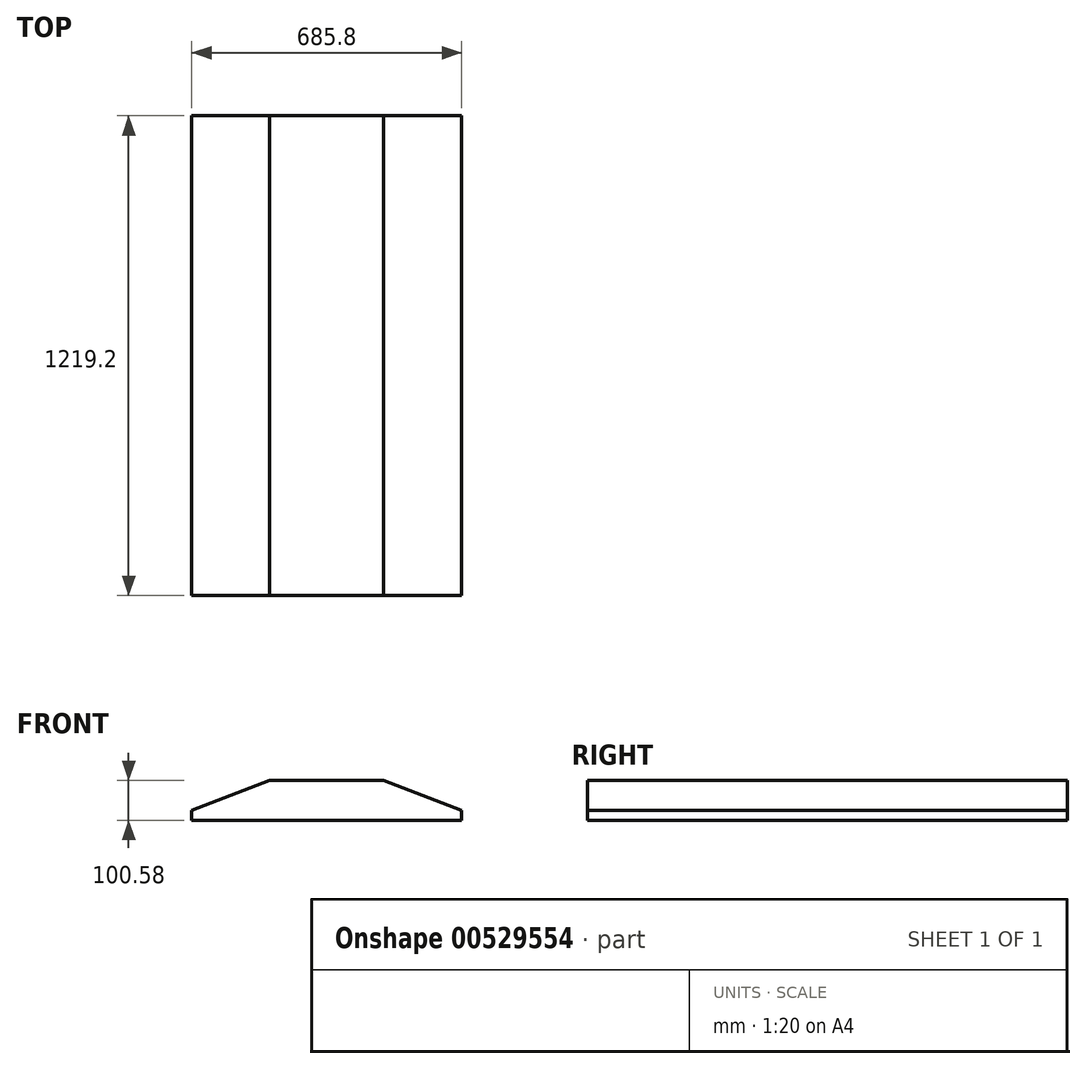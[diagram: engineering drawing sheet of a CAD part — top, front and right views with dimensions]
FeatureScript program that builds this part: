
annotation { "Feature Type Name" : "Feature", "Feature Type Description" : "" }
export const myFeature = defineFeature(function(context is Context, id is Id, definition is map)
    precondition{}
    {
        {
            var Q0;
            Q0=qCreatedBy(makeId("Top.planeOp"),FACE);
            var sketch = newSketch(context, id + "F0", { "sketchPlane" : qUnion([Q0])});
            skLineSegment(sketch, "E0.bottom", {"start": v(-362.06, 514.95) * mm, "end": v(323.74, 514.95) * mm});
            skLineSegment(sketch, "E0.top", {"start": v(-362.06, -704.25) * mm, "end": v(323.74, -704.25) * mm});
            skLineSegment(sketch, "E0.left", {"start": v(-362.06, 514.95) * mm, "end": v(-362.06, -704.25) * mm});
            skLineSegment(sketch, "E0.right", {"start": v(323.74, 514.95) * mm, "end": v(323.74, -704.25) * mm});
            skSolve(sketch);
        }
        {
            var Q0;
            Q0=makeQuery(id+"F0.imprint","IMPRINT",FACE,{"disambiguationData":[TD([[makeQuery(id+"F0.imprint","IMPRINT",EDGE,{"derivedFrom":sQuery(id+"F0.wireOp",EDGE,"E0.bottom")}),-1.0]])]});
            extrude(context, id + "F1", {"entities" : qUnion([Q0]), "depth" : 100.58 * mm, "offsetDistance" : 30.48 * mm});
        }
        {
            var Q0;
            Q0=makeQuery(id+"F1.opExtrude","CAP_EDGE",EDGE,{"disambiguationData":[OSD([sQuery(id+"F0.wireOp",EDGE,"E0.left")])],"isStart":false});
            chamfer(context, id + "F2", {"entities" : qUnion([Q0]), "chamferType" : ChamferType.TWO_OFFSETS, "width1" : 198.12 * mm, "oppositeDirection" : false, "width2" : 76.2 * mm, "tangentPropagation" : true});
        }
        {
            var Q0;
            Q0=makeQuery(id+"F1.opExtrude","CAP_EDGE",EDGE,{"disambiguationData":[OSD([sQuery(id+"F0.wireOp",EDGE,"E0.right")])],"isStart":false});
            chamfer(context, id + "F3", {"entities" : qUnion([Q0]), "chamferType" : ChamferType.TWO_OFFSETS, "width1" : 76.2 * mm, "oppositeDirection" : false, "width2" : 198.12 * mm, "tangentPropagation" : true});
        }
    });
